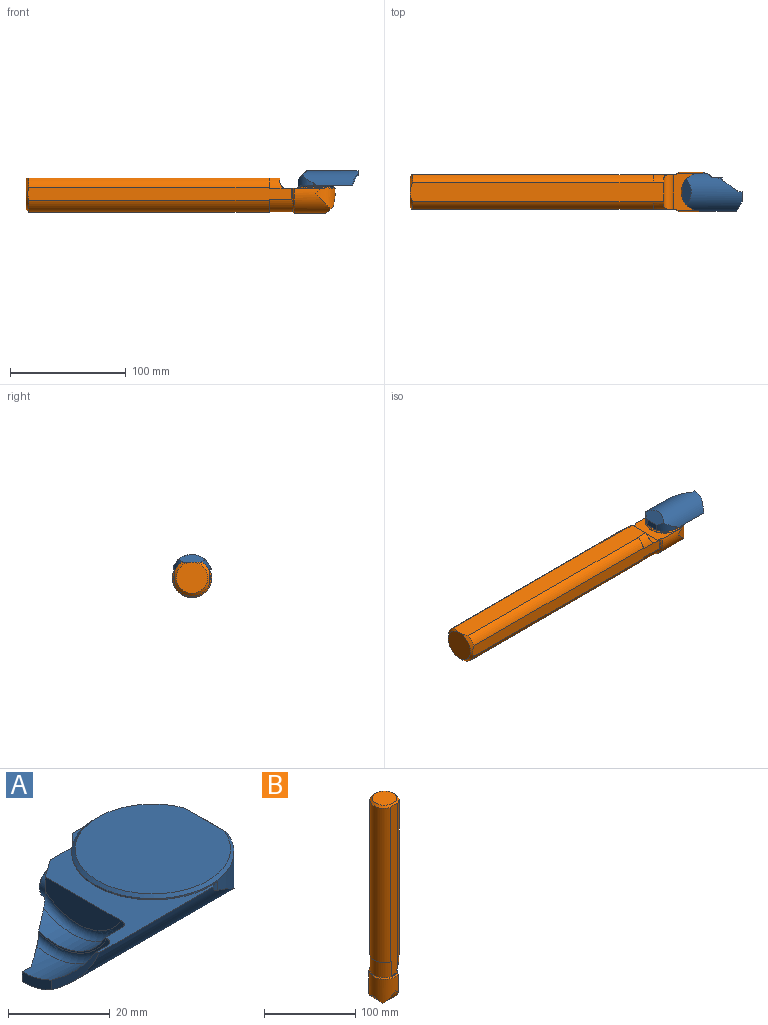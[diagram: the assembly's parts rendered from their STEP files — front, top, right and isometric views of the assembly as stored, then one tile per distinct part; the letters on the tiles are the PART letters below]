
ASSEMBLY  parts=2 mates=1
PART A: 37 faces, bbox 52.2x34.1x14.9 mm
  f0: cylinder r=17.3mm len=47.97mm, axis (-1,0,0), area 1512.1mm2, adj f1,f2,f3,f4,f5,f6,f7,f8
  f1: plane 18.2x13.03mm, normal (-0.57,0.82,0), area 86.3mm2, adj f0,f7,f12,f13,f14,f15,f16,f17
  f2: cylinder r=16mm len=32mm, axis (0,0,1), area 249mm2, adj f0,f3,f6,f9,f10,f20,f21,f22
  f3: cylinder r=5mm len=2.21mm, axis (0,0,1), area 2.4mm2, adj f0,f2,f20
  f4: plane 11.45x9.12mm, normal (-0.87,-0.5,0), area 20.7mm2, adj f0,f8,f17,f20
  f5: plane 7.95x3.86mm, normal (-0.71,0.71,0), area 25.2mm2, adj f0,f6,f7,f22
  f6: plane 6.46x2.34mm, normal (0,1,0), area 15.1mm2, adj f0,f2,f5,f22
  f7: plane 9.14x7.77mm, normal (0,1,0), area 53.7mm2, adj f0,f1,f5,f19,f20,f24,f25,f33
  f8: plane 8.28x4.52mm, normal (-1,0,0), area 19.8mm2, adj f0,f4,f17,f18
  f9: plane 22.9x8.19mm, normal (0.71,0,-0.71), area 175.6mm2, adj f0,f2,f10
  f10: plane 11.14x5.52mm, normal (1,0,0), area 61.5mm2, adj f2,f9,f11
  f11: plane 11.14x0.68mm, normal (0.71,0,0.71), area 10.5mm2, adj f10,f21,f23
  f12: torus R=16mm, axis (-1,0,0), area 59mm2, adj f1,f14,f17,f20
  f13: cylinder r=15.6mm len=21.84mm, axis (-1,0,0), area 111mm2, adj f1,f14,f15,f20
  f14: plane 18.99x8.82mm, normal (-1,0,0), area 8.9mm2, adj f1,f12,f13,f20
  f15: torus R=14mm, axis (-1,0,0), area 63.6mm2, adj f1,f13,f16,f20
  f16: plane 21.13x6.82mm, normal (-1,0,0), area 110.5mm2, adj f1,f15,f20
  f17: cylinder r=17.6mm len=19.64mm, axis (-1,0,0), area 141.3mm2, adj f1,f4,f8,f12,f18,f20
  f18: plane 2.55x2.4mm, normal (0,1,0), area 6.1mm2, adj f0,f1,f8,f17
  f19: plane 4.27x2.41mm, normal (-0.57,0.82,0), area 5.9mm2, adj f7,f24,f25,f26,f27,f28,f29,f30
  f20: plane 34.57x29.61mm, normal (0,0,1), area 241.4mm2, adj f0,f1,f2,f3,f4,f7,f12,f13
  f21: cone r=16mm half-angle=45deg, axis (0,0,-1), area 83.3mm2, adj f2,f11,f23
  f22: plane 9.86x3.4mm, normal (0,0,1), area 4.9mm2, adj f2,f5,f6
  f23: plane 30.65x29.65mm, normal (0,0,1), area 730.5mm2, adj f11,f21
  f24: cone r=1.42mm half-angle=60deg, axis (0,1,0), area 0.3mm2, adj f7,f19,f31,f32
  f25: cone r=1.42mm half-angle=60deg, axis (0,1,0), area 0.3mm2, adj f7,f19,f29,f30
  f26: cylinder r=0.83mm len=1.15mm, axis (0,1,0), area 1.2mm2, adj f19,f27,f32,f35
  f27: cylinder r=0.33mm len=1.28mm, axis (0,1,0), area 1mm2, adj f19,f26,f28,f35,f36
  f28: cylinder r=0.83mm len=1.15mm, axis (0,1,0), area 1.2mm2, adj f19,f27,f29,f36
  f29: cylinder r=0.33mm len=0.87mm, axis (0,1,0), area 0.5mm2, adj f19,f25,f28,f30,f36
  f30: cylinder r=0.83mm len=0.36mm, axis (0,1,0), area 0.1mm2, adj f19,f25,f29
  f31: cylinder r=0.83mm len=0.36mm, axis (0,1,0), area 0.1mm2, adj f19,f24,f32
  f32: cylinder r=0.33mm len=0.87mm, axis (0,1,0), area 0.5mm2, adj f19,f24,f26,f31,f35
  f33: cone r=3mm half-angle=45deg, axis (0,-1,0), area 8mm2, adj f0,f1,f7,f34
  f34: cylinder r=3.5mm len=6.95mm, axis (0,-1,0), area 12.9mm2, adj f0,f1,f33
  f35: cone r=1.42mm half-angle=60deg, axis (0,1,0), area 0.7mm2, adj f7,f26,f27,f32
  f36: cone r=1.42mm half-angle=60deg, axis (0,1,0), area 0.7mm2, adj f7,f27,f28,f29
PART B: 27 faces, bbox 35.8x36.8x269.8 mm
  f0: cylinder r=15.68mm len=13.67mm, axis (0,0,1), area 120.6mm2, adj f5,f16,f17,f22,f26
  f1: cylinder r=15.68mm len=13.67mm, axis (0,0,1), area 120.6mm2, adj f4,f16,f17,f24,f26
  f2: cylinder r=16mm len=207.18mm, axis (0,0,1), area 2150.7mm2, adj f4,f13,f24,f26
  f3: cylinder r=16mm len=207.18mm, axis (0,0,1), area 2150.7mm2, adj f5,f13,f22,f26
  f4: cone r=15.68mm half-angle=45deg, axis (0,0,1), area 5.1mm2, adj f1,f2,f24,f26
  f5: cone r=15.68mm half-angle=45deg, axis (0,0,1), area 5.1mm2, adj f0,f3,f22,f26
  f6: cylinder r=17mm len=34mm, axis (0,0,-1), area 1634.3mm2, adj f7,f9,f15,f18
  f7: cylinder r=17mm len=34mm, axis (1,0,0), area 575.4mm2, adj f6,f10,f15,f18
  f8: cylinder r=15.68mm len=31.35mm, axis (0,0,1), area 812.7mm2, adj f9,f14,f17,f18,f22,f23,f24,f25
  f9: cone r=15.68mm half-angle=45deg, axis (0,0,-1), area 114.8mm2, adj f6,f8,f18
  f10: plane 15.9x11.19mm, normal (-0.17,0,-0.98), area 122mm2, adj f7,f15
  f11: cylinder r=16mm len=207.18mm, axis (0,0,1), area 8057.5mm2, adj f13,f14,f22,f24
  f12: plane 27x27mm, normal (0,0,1), area 572.6mm2, adj f13
  f13: cone r=16mm half-angle=45deg, axis (0,0,-1), area 297.3mm2, adj f2,f3,f11,f12,f22,f24,f26
  f14: cone r=15.68mm half-angle=45deg, axis (0,0,1), area 18.1mm2, adj f8,f11,f22,f24
  f15: cylinder r=20mm len=21.57mm, axis (0,-1,0), area 147.9mm2, adj f6,f7,f10
  f16: plane 23.46x3.1mm, normal (0,0,-1), area 62.3mm2, adj f0,f1,f17,f26
  f17: cylinder r=6mm len=30mm, axis (0,-1,0), area 339.1mm2, adj f0,f1,f8,f16,f18,f22,f24
  f18: plane 39.62x32.57mm, normal (1,0,0), area 371.8mm2, adj f6,f7,f8,f9,f17,f19
  f19: cylinder r=16mm len=32mm, axis (-1,0,0), area 33.2mm2, adj f18,f21
  f20: plane 30x30mm, normal (1,0,0), area 706.9mm2, adj f21
  f21: cone r=15mm half-angle=45deg, axis (-1,0,0), area 137.7mm2, adj f19,f20
  f22: plane 230.33x13.96mm, normal (0,-1,0), area 2490.3mm2, adj f0,f3,f5,f8,f11,f13,f14,f17
  f23: plane 9.1x0.68mm, normal (0,-0.71,0.71), area 5.8mm2, adj f8,f22
  f24: plane 230.33x13.96mm, normal (0,1,0), area 2490.3mm2, adj f1,f2,f4,f8,f11,f13,f14,f17
  f25: plane 9.1x0.68mm, normal (0,0.71,0.71), area 5.8mm2, adj f8,f24
  f26: plane 220.82x19mm, normal (1,0,0), area 3735.1mm2, adj f0,f1,f2,f3,f4,f5,f13,f16
PLACE A rot(axis=(0,1,0),180deg) t=(-6.46,-10.22,92.5)mm
PLACE B rot(axis=(0,-1,0),90deg) t=(-256.46,-10.22,86.27)mm
MATE fastened B.f7 <-> A.f2  axis (0,0,1) through (-6.46,-10.22,92.5)mm
